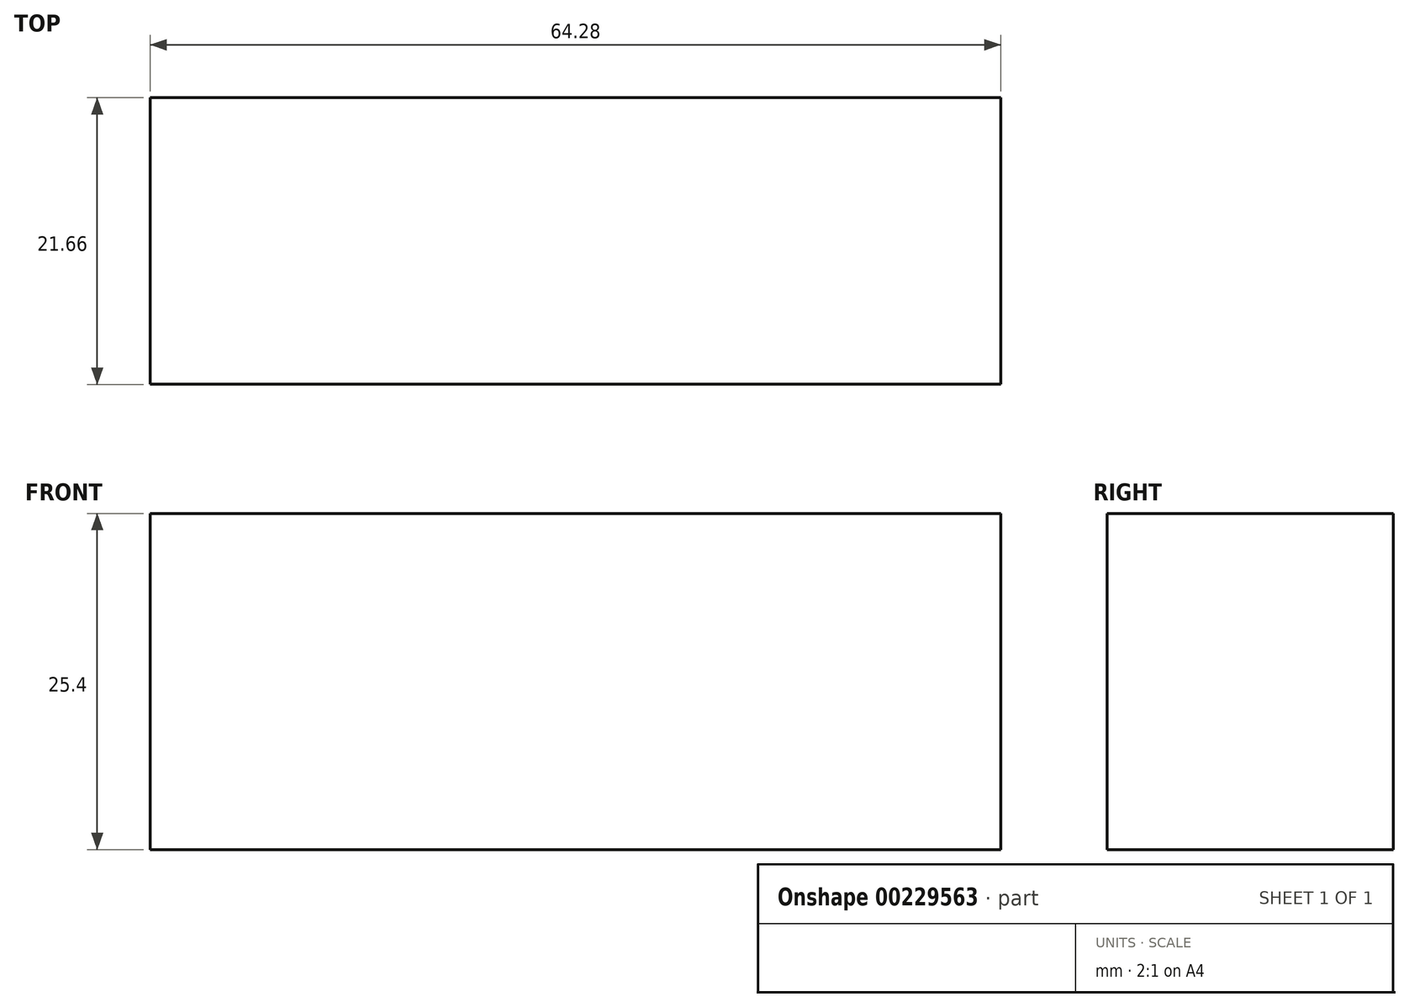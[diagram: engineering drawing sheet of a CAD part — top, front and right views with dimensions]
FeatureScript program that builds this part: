
annotation { "Feature Type Name" : "Feature", "Feature Type Description" : "" }
export const myFeature = defineFeature(function(context is Context, id is Id, definition is map)
    precondition{}
    {
        {
            var Q0;
            Q0=qCreatedBy(makeId("Top.planeOp"),FACE);
            var sketch = newSketch(context, id + "F0", { "sketchPlane" : qUnion([Q0])});
            skLineSegment(sketch, "E0.bottom", {"start": v(-32.14, 10.83) * mm, "end": v(32.14, 10.83) * mm});
            skLineSegment(sketch, "E0.top", {"start": v(-32.14, -10.83) * mm, "end": v(32.14, -10.83) * mm});
            skLineSegment(sketch, "E0.left", {"start": v(-32.14, 10.83) * mm, "end": v(-32.14, -10.83) * mm});
            skLineSegment(sketch, "E0.right", {"start": v(32.14, 10.83) * mm, "end": v(32.14, -10.83) * mm});
            skPoint(sketch, "E0.middle", {"position": v(0, 0) * mm});
            skSolve(sketch);
        }
        {
            var Q0;
            Q0=makeQuery(id+"F0.imprint","IMPRINT",FACE,{"disambiguationData":[TD([[makeQuery(id+"F0.imprint","IMPRINT",EDGE,{"derivedFrom":sQuery(id+"F0.wireOp",EDGE,"E0.bottom")}),-1.0]])]});
            extrude(context, id + "F1", {"entities" : qUnion([Q0]), "depth" : 25.4 * mm});
        }
    });
